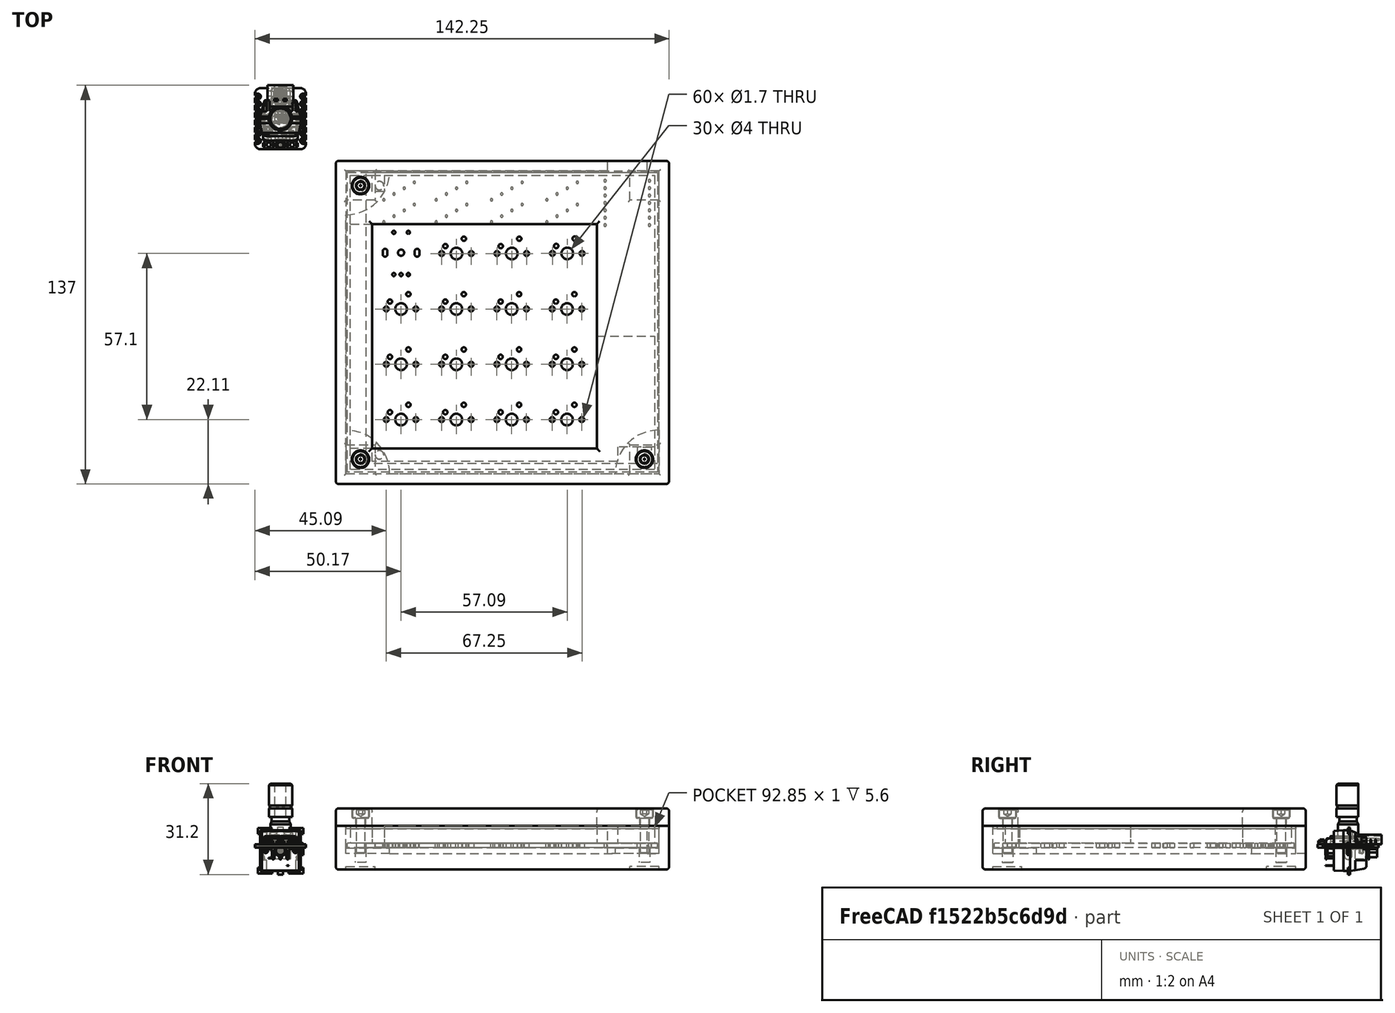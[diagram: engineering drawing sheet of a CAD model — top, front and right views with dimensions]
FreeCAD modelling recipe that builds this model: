
FCSTD DOCUMENT  (FreeCAD 1.0R39109 (Git))
Label: case
License: All rights reserved
LicenseURL: http://en.wikipedia.org/wiki/All_rights_reserved
objects: App::Part×69, Part::Feature×68, Sketcher::SketchObject×13, PartDesign::Pad×10, Part::FeaturePython×3, PartDesign::Fillet×3, PartDesign::ShapeBinder×2, PartDesign::Hole×2, PartDesign::Body×2, PartDesign::Pocket×1
note: 149 computed .brp shape members not serialized (recipe doc carries the construction recipe); baked Part::Feature solids carry a one-line shape summary decoded from their .brp

FEATURE [PartDesign::ShapeBinder] ShapeBinder
  TraceSupport = false
FEATURE [Sketcher::SketchObject] Sketch
  ArcFitTolerance = 1e-06
  AttachmentSupport = -> [XY_Plane]
  ExternalGeometry = -> [ShapeBinder]
  FullyConstrained = true
  MakeInternals = false
  MapMode = 5
  sketch-geometry (26):
    g0: LineSegment StartX=19 StartY=-14.5 StartZ=0 EndX=19 EndY=-125.5 EndZ=0
    g1: LineSegment StartX=19 StartY=-125.5 StartZ=0 EndX=133.5 EndY=-125.5 EndZ=0
    g2: LineSegment StartX=133.5 StartY=-125.5 StartZ=0 EndX=133.5 EndY=-14.5 EndZ=0
    g3: LineSegment StartX=133.5 StartY=-14.5 StartZ=0 EndX=125.925 EndY=-14.5 EndZ=0
    g4: LineSegment StartX=22.5 StartY=-18 StartZ=0 EndX=22.5 EndY=-122 EndZ=0
    g5: LineSegment StartX=22.5 StartY=-122 StartZ=0 EndX=130 EndY=-122 EndZ=0
    g6: LineSegment StartX=130 StartY=-122 StartZ=0 EndX=130 EndY=-18 EndZ=0
    g7: LineSegment StartX=130 StartY=-18 StartZ=0 EndX=125.925 EndY=-18 EndZ=0
    g8: LineSegment [constr] StartX=112.425 StartY=-8.5 StartZ=0 EndX=112.425 EndY=-18.5 EndZ=0
    g9: LineSegment [constr] StartX=112.425 StartY=-18.5 StartZ=0 EndX=125.925 EndY=-18.5 EndZ=0
    g10: LineSegment [constr] StartX=125.925 StartY=-18.5 StartZ=0 EndX=125.925 EndY=-8.5 EndZ=0
    g11: LineSegment [constr] StartX=125.925 StartY=-8.5 StartZ=0 EndX=112.425 EndY=-8.5 EndZ=0
    g12: LineSegment [constr] StartX=110.5 StartY=-18.5 StartZ=0 EndX=129.5 EndY=-18.5 EndZ=0
    g13: GeomPoint [constr] X=119.175 Y=-18.5 Z=0
    g14: GeomPoint [constr] X=120 Y=-18.5 Z=0
    g15: GeomPoint [constr] X=127.85 Y=-18.5 Z=0
    g16: LineSegment [constr] StartX=112.425 StartY=-18.5 StartZ=0 EndX=110.5 EndY=-18.5 EndZ=0
    g17: LineSegment [constr] StartX=125.925 StartY=-18.5 StartZ=0 EndX=127.85 EndY=-18.5 EndZ=0
    g18: LineSegment [constr] StartX=110.5 StartY=-18.5 StartZ=0 EndX=112.425 EndY=-18.5 EndZ=0
    g19: LineSegment [constr] StartX=125.925 StartY=-18.5 StartZ=0 EndX=127.85 EndY=-18.5 EndZ=0
    g20: LineSegment [constr] StartX=110.5 StartY=-18.5 StartZ=0 EndX=112.425 EndY=-18.5 EndZ=0
    g21: LineSegment [constr] StartX=125.925 StartY=-18.5 StartZ=0 EndX=127.85 EndY=-18.5 EndZ=0
    g22: LineSegment StartX=112.425 StartY=-14.5 StartZ=0 EndX=19 EndY=-14.5 EndZ=0
    g23: LineSegment StartX=112.425 StartY=-18 StartZ=0 EndX=22.5 EndY=-18 EndZ=0
    g24: LineSegment StartX=112.425 StartY=-18 StartZ=0 EndX=112.425 EndY=-14.5 EndZ=0
    g25: LineSegment StartX=125.925 StartY=-18 StartZ=0 EndX=125.925 EndY=-14.5 EndZ=0
  constraints (69):
    c: Coincident(g0,g1)
    c: Coincident(g1,g2)
    c: Coincident(g2,g3)
    c: Coincident(g22,g0)
    c: Vertical(g0)
    c: Vertical(g2)
    c: Horizontal(g1)
    c: Horizontal(g3)
    c: Distance(g-6,g2) = 4
    c: DistanceX(g0,g-4) = 4
    c: Distance(g3,g-3) = 4
    c: Distance(g-5,g1) = 4
    c: Coincident(g4,g5)
    c: Coincident(g5,g6)
    c: Coincident(g6,g7)
    c: Coincident(g23,g4)
    c: Vertical(g4)
    c: Vertical(g6)
    c: Horizontal(g5)
    c: Horizontal(g7)
    c: DistanceY(g5,g-6) = 0.5
    c: Distance(g-6,g6) = 0.5
    c: Distance(g7,g-3) = 0.5
    c: Distance(g4,g-4) = 0.5
    c: Coincident(g8,g9)
    c: Coincident(g9,g10)
    c: Coincident(g10,g11)
    c: Coincident(g11,g8)
    c: Vertical(g8)
    c: Vertical(g10)
    c: Horizontal(g9)
    c: Horizontal(g11)
    c: PointOnObject(g9,g-3)
    c: DistanceX(g11,g11) = 13.5
    c: PointOnObject(g12,g-3)
    c: Coincident(g12,g-6)
    c: Symmetric(g9,g9,g13)
    c: DistanceX(g12,g12) = 19
    c: Symmetric(g12,g12,g14)
    c: PointOnObject(g15,g12)
    c: DistanceX(g15,g12) = 1.65
    c: Coincident(g16,g8)
    c: Coincident(g16,g12)
    c: Coincident(g17,g9)
    c: Coincident(g17,g15)
    c: Coincident(g18,g12)
    c: Coincident(g18,g8)
    c: Coincident(g19,g9)
    c: Coincident(g19,g15)
    c: PointOnObject(g20,g8)
    c: Horizontal(g20)
    c: PointOnObject(g21,g10)
    c: Horizontal(g21)
    c: Equal(g21,g20)
    c: Coincident(g21,g15)
    c: Coincident(g20,g12)
    c: DistanceY(g8,g8) = 10
    c: PointOnObject(g3,g10)
    c: PointOnObject(g22,g8)
    c: PointOnObject(g7,g10)
    c: PointOnObject(g23,g8)
    c: Coincident(g24,g23)
    c: Coincident(g24,g22)
    c: Coincident(g25,g7)
    c: Coincident(g25,g3)
    c: Horizontal(g22,g3)
    c: Horizontal(g23,g7)
    c: Horizontal(g23)
    c: Horizontal(g22)
FEATURE [PartDesign::Pad] Pad
  Direction = (0,0,1)
  Length = 15
  Length2 = 10
  Midplane = true
  Profile = -> Sketch
  ReferenceAxis = -> Sketch [N_Axis]
  Suppressed = false
  Type = 0
FEATURE [Sketcher::SketchObject] Sketch001
  ArcFitTolerance = 1e-06
  AttachmentSupport = -> [Pad]
  ExternalGeometry = -> [Pad]
  FullyConstrained = true
  MakeInternals = false
  MapMode = 5
  Placement = pos=(0,-122,0) rot=(0,0.707107,0.707107;3.14159rad)
  sketch-geometry (5):
    g0: GeomPoint X=0 Y=-2 Z=0
    g1: LineSegment StartX=-130 StartY=-7.5 StartZ=0 EndX=-22.5 EndY=-7.5 EndZ=0
    g2: LineSegment StartX=-22.5 StartY=-7.5 StartZ=0 EndX=-22.5 EndY=-2 EndZ=0
    g3: LineSegment StartX=-22.5 StartY=-2 StartZ=0 EndX=-130 EndY=-2 EndZ=0
    g4: LineSegment StartX=-130 StartY=-2 StartZ=0 EndX=-130 EndY=-7.5 EndZ=0
  constraints (13):
    c: PointOnObject(g0,g-2)
    c: DistanceY(g0,g-1) = 2
    c: Coincident(g1,g2)
    c: Coincident(g2,g3)
    c: Coincident(g3,g4)
    c: Coincident(g4,g1)
    c: Horizontal(g1)
    c: Horizontal(g3)
    c: Vertical(g2)
    c: Vertical(g4)
    c: Coincident(g1,g-3)
    c: PointOnObject(g2,g-4)
    c: Horizontal(g0,g2)
FEATURE [PartDesign::Pad] Pad001
  BaseFeature = -> Pad
  Direction = (0,1,-2e-16)
  Length = 10
  Length2 = 10
  Profile = -> Sketch001
  ReferenceAxis = -> Sketch001 [N_Axis]
  Suppressed = false
  Type = 3
  UpToFace = -> Pad [Face2]
FEATURE [Sketcher::SketchObject] Sketch002
  ArcFitTolerance = 1e-06
  AttachmentSupport = -> [Pad001]
  ExternalGeometry = -> [Pad001]
  FullyConstrained = true
  MakeInternals = false
  MapMode = 5
  Placement = pos=(0,-4e-16,-2) rot=(0,0,1;0rad)
  sketch-geometry (9):
    g0: ArcOfCircle CenterX=130 CenterY=-122 CenterZ=0 NormalX=0 NormalY=0 NormalZ=1 AngleXU=0 Radius=15 StartAngle=1.5708 EndAngle=3.14159
    g1: ArcOfCircle CenterX=22.5 CenterY=-122 CenterZ=0 NormalX=0 NormalY=0 NormalZ=1 AngleXU=0 Radius=15 StartAngle=0 EndAngle=1.5708
    g2: ArcOfCircle CenterX=22.5 CenterY=-18 CenterZ=0 NormalX=0 NormalY=0 NormalZ=1 AngleXU=0 Radius=15 StartAngle=4.71239 EndAngle=6.28319
    g3: LineSegment StartX=37.5 StartY=-18 StartZ=0 EndX=22.5 EndY=-18 EndZ=0
    g4: LineSegment StartX=22.5 StartY=-18 StartZ=0 EndX=22.5 EndY=-33 EndZ=0
    g5: LineSegment StartX=22.5 StartY=-122 StartZ=0 EndX=22.5 EndY=-107 EndZ=0
    g6: LineSegment StartX=22.5 StartY=-122 StartZ=0 EndX=37.5 EndY=-122 EndZ=0
    g7: LineSegment StartX=130 StartY=-107 StartZ=0 EndX=130 EndY=-122 EndZ=0
    g8: LineSegment StartX=115 StartY=-122 StartZ=0 EndX=130 EndY=-122 EndZ=0
  constraints (24):
    c: Coincident(g0,g-6)
    c: PointOnObject(g0,g-6)
    c: PointOnObject(g0,g-5)
    c: Radius(g1) = 15
    c: Angle(g1) = 1.5708
    c: Coincident(g1,g-5)
    c: PointOnObject(g1,g-5)
    c: Equal(g0,g1)
    c: Coincident(g2,g-4)
    c: PointOnObject(g2,g-3)
    c: PointOnObject(g2,g-4)
    c: Equal(g2,g1)
    c: Coincident(g2,g3)
    c: Coincident(g3,g2)
    c: Coincident(g3,g4)
    c: Coincident(g4,g2)
    c: Coincident(g5,g1)
    c: Coincident(g5,g1)
    c: Coincident(g6,g1)
    c: Coincident(g6,g1)
    c: Coincident(g7,g0)
    c: Coincident(g7,g0)
    c: Coincident(g8,g0)
    c: Coincident(g8,g0)
FEATURE [PartDesign::Pad] Pad002
  BaseFeature = -> Pad001
  Direction = (0,0,1)
  Length = 1.9
  Length2 = 10
  Profile = -> Sketch002
  ReferenceAxis = -> Sketch002 [N_Axis]
  Suppressed = false
  Type = 0
FEATURE [Sketcher::SketchObject] Sketch003
  ArcFitTolerance = 1e-06
  AttachmentSupport = -> [Pad002]
  ExternalGeometry = -> [Pad002]
  FullyConstrained = true
  MakeInternals = false
  MapMode = 5
  Placement = pos=(0,0,-0.1) rot=(0,0,1;0rad)
  sketch-geometry (3):
    g0: Circle CenterX=27.5 CenterY=-23 CenterZ=0 NormalX=0 NormalY=0 NormalZ=1 AngleXU=0 Radius=1.5
    g1: Circle CenterX=27.5 CenterY=-117 CenterZ=0 NormalX=0 NormalY=0 NormalZ=1 AngleXU=0 Radius=1.5
    g2: Circle CenterX=125 CenterY=-117 CenterZ=0 NormalX=0 NormalY=0 NormalZ=1 AngleXU=0 Radius=1.5
  constraints (9):
    c: DistanceY(g0,g-5) = 5
    c: DistanceX(g-5,g0) = 5
    c: Horizontal(g2,g1)
    c: Vertical(g1,g0)
    c: Distance(g1,g-6) = 5
    c: Distance(g2,g-7) = 5
    c: Diameter(g2) = 3
    c: Equal(g2,g1)
    c: Equal(g1,g0)
FEATURE [Part::Feature] Part__Feature034  label="D_DO-35_SOD27_P7.62mm_Horizontal032"
  shape: bbox 8.244 x 2.165 x 5.082 mm, 16 faces, 2 solids (baked)
FEATURE [App::Part] D_DO_35_SOD27_P7_62mm_Horizontal016  label="D_DO-35_SOD27_P7.62mm_Horizontal033"
  Group = -> [Part__Feature034]
  Origin = -> Origin035
  Placement = pos=(53.5,-35.5,1.65) rot=(0,0,1;1.5708rad)
FEATURE [Part::Feature] Part__Feature035  label="cherry mx v043"
  shape: bbox 15.64 x 17.69 x 16.33 mm, 129 faces, 8 solids (baked)
FEATURE [App::Part] cherryMX015
  Group = -> [Part__Feature035]
  Origin = -> Origin036
  Placement = pos=(79.46,-104.31,6.65) rot=(1,0,0;1.5708rad)
FEATURE [Part::Feature] Part__Feature036  label="D_DO-35_SOD27_P7.62mm_Horizontal034"
  shape: bbox 8.244 x 2.165 x 5.082 mm, 16 faces, 2 solids (baked)
FEATURE [App::Part] D_DO_35_SOD27_P7_62mm_Horizontal017  label="D_DO-35_SOD27_P7.62mm_Horizontal035"
  Group = -> [Part__Feature036]
  Origin = -> Origin037
  Placement = pos=(83,-29.5,1.65) rot=(0,0,1;1.5708rad)
FEATURE [Part::Feature] Part__Feature037  label="D_DO-35_SOD27_P7.62mm_Horizontal036"
  shape: bbox 8.244 x 2.165 x 5.082 mm, 16 faces, 2 solids (baked)
FEATURE [App::Part] D_DO_35_SOD27_P7_62mm_Horizontal018  label="D_DO-35_SOD27_P7.62mm_Horizontal037"
  Group = -> [Part__Feature037]
  Origin = -> Origin038
  Placement = pos=(64,-29.5,1.65) rot=(0,0,1;1.5708rad)
FEATURE [Part::Feature] Part__Feature038  label="D_DO-35_SOD27_P7.62mm_Horizontal038"
  shape: bbox 8.244 x 2.165 x 5.082 mm, 16 faces, 2 solids (baked)
FEATURE [App::Part] D_DO_35_SOD27_P7_62mm_Horizontal019  label="D_DO-35_SOD27_P7.62mm_Horizontal039"
  Group = -> [Part__Feature038]
  Origin = -> Origin039
  Placement = pos=(39,-33.5,1.65) rot=(0,0,1;1.5708rad)
FEATURE [Part::Feature] Part__Feature039  label="D_DO-35_SOD27_P7.62mm_Horizontal040"
  shape: bbox 8.244 x 2.165 x 5.082 mm, 16 faces, 2 solids (baked)
FEATURE [App::Part] D_DO_35_SOD27_P7_62mm_Horizontal020  label="D_DO-35_SOD27_P7.62mm_Horizontal041"
  Group = -> [Part__Feature039]
  Origin = -> Origin040
  Placement = pos=(57,-33.5,1.65) rot=(0,0,1;1.5708rad)
FEATURE [Part::Feature] Part__Feature040  label="cherry mx v044"
  shape: bbox 15.64 x 17.69 x 16.33 mm, 129 faces, 8 solids (baked)
FEATURE [App::Part] cherryMX016
  Group = -> [Part__Feature040]
  Origin = -> Origin041
  Placement = pos=(79.5,-47.25,6.65) rot=(1,0,0;1.5708rad)
FEATURE [Part::Feature] Part__Feature041  label="cherry mx v045"
  shape: bbox 15.64 x 17.69 x 16.33 mm, 129 faces, 8 solids (baked)
FEATURE [App::Part] cherryMX017
  Group = -> [Part__Feature041]
  Origin = -> Origin042
  Placement = pos=(79.46,-85.31,6.65) rot=(1,0,0;1.5708rad)
FEATURE [Part::Feature] Part__Feature042  label="D_DO-35_SOD27_P7.62mm_Horizontal042"
  shape: bbox 8.244 x 2.165 x 5.082 mm, 16 faces, 2 solids (baked)
FEATURE [App::Part] D_DO_35_SOD27_P7_62mm_Horizontal021  label="D_DO-35_SOD27_P7.62mm_Horizontal043"
  Group = -> [Part__Feature042]
  Origin = -> Origin043
  Placement = pos=(98.5,-31.5,1.65) rot=(0,0,1;1.5708rad)
FEATURE [Part::Feature] Part__Feature043  label="D_DO-35_SOD27_P7.62mm_Horizontal044"
  shape: bbox 8.244 x 2.165 x 5.082 mm, 16 faces, 2 solids (baked)
FEATURE [App::Part] D_DO_35_SOD27_P7_62mm_Horizontal022  label="D_DO-35_SOD27_P7.62mm_Horizontal045"
  Group = -> [Part__Feature043]
  Origin = -> Origin044
  Placement = pos=(60.5,-31.5,1.65) rot=(0,0,1;1.5708rad)
FEATURE [Part::Feature] Part__Feature044  label="D_DO-35_SOD27_P7.62mm_Horizontal046"
  shape: bbox 8.244 x 2.165 x 5.082 mm, 16 faces, 2 solids (baked)
FEATURE [App::Part] D_DO_35_SOD27_P7_62mm_Horizontal023  label="D_DO-35_SOD27_P7.62mm_Horizontal047"
  Group = -> [Part__Feature044]
  Origin = -> Origin045
  Placement = pos=(46,-29.5,1.65) rot=(0,0,1;1.5708rad)
FEATURE [Part::Feature] Part__Feature045  label="cherry mx v046"
  shape: bbox 15.64 x 17.69 x 16.33 mm, 129 faces, 8 solids (baked)
FEATURE [App::Part] cherryMX018
  Group = -> [Part__Feature045]
  Origin = -> Origin046
  Placement = pos=(60.46,-66.31,6.65) rot=(1,0,0;1.5708rad)
FEATURE [Part::Feature] Part__Feature046  label="cherry mx v047"
  shape: bbox 15.64 x 17.69 x 16.33 mm, 129 faces, 8 solids (baked)
FEATURE [App::Part] cherryMX019
  Group = -> [Part__Feature046]
  Origin = -> Origin047
  Placement = pos=(98.55,-47.21,6.65) rot=(1,0,0;1.5708rad)
FEATURE [Part::Feature] Part__Feature047  label="D_DO-35_SOD27_P7.62mm_Horizontal048"
  shape: bbox 8.244 x 2.165 x 5.082 mm, 16 faces, 2 solids (baked)
FEATURE [App::Part] D_DO_35_SOD27_P7_62mm_Horizontal024  label="D_DO-35_SOD27_P7.62mm_Horizontal049"
  Group = -> [Part__Feature047]
  Origin = -> Origin048
  Placement = pos=(42.5,-31.5,1.65) rot=(0,0,1;1.5708rad)
FEATURE [Part::Feature] Part__Feature048  label="cherry mx v048"
  shape: bbox 15.64 x 17.69 x 16.33 mm, 129 faces, 8 solids (baked)
FEATURE [App::Part] cherryMX020
  Group = -> [Part__Feature048]
  Origin = -> Origin049
  Placement = pos=(98.46,-85.31,6.65) rot=(1,0,0;1.5708rad)
FEATURE [Part::Feature] Part__Feature049  label="D_DO-35_SOD27_P7.62mm_Horizontal050"
  shape: bbox 8.244 x 2.165 x 5.082 mm, 16 faces, 2 solids (baked)
FEATURE [App::Part] D_DO_35_SOD27_P7_62mm_Horizontal025  label="D_DO-35_SOD27_P7.62mm_Horizontal051"
  Group = -> [Part__Feature049]
  Origin = -> Origin050
  Placement = pos=(102,-29.5,1.65) rot=(0,0,1;1.5708rad)
FEATURE [Part::Feature] Part__Feature050  label="D_DO-35_SOD27_P7.62mm_Horizontal052"
  shape: bbox 8.244 x 2.165 x 5.082 mm, 16 faces, 2 solids (baked)
FEATURE [App::Part] D_DO_35_SOD27_P7_62mm_Horizontal026  label="D_DO-35_SOD27_P7.62mm_Horizontal053"
  Group = -> [Part__Feature050]
  Origin = -> Origin051
  Placement = pos=(76,-33.5,1.65) rot=(0,0,1;1.5708rad)
FEATURE [Part::Feature] Part__Feature051  label="Seeed Studio XIAO RP2040 v027"
  shape: bbox 17.5 x 22 x 4.405 mm, 1237 faces, 83 solids (baked)
FEATURE [App::Part] Seeed_Studio_XIAO_RP2041  label="Seeed Studio XIAO RP2041"
  Group = -> [Part__Feature051]
  Origin = -> Origin052
  Placement = pos=(119.12,-28.96,1.65) rot=(0,0,1;0rad)
FEATURE [Part::Feature] Part__Feature052  label="cherry mx v049"
  shape: bbox 15.64 x 17.69 x 16.33 mm, 129 faces, 8 solids (baked)
FEATURE [App::Part] cherryMX021
  Group = -> [Part__Feature052]
  Origin = -> Origin053
  Placement = pos=(41.46,-66.31,6.65) rot=(1,0,0;1.5708rad)
FEATURE [Part::Feature] Part__Feature053  label="D_DO-35_SOD27_P7.62mm_Horizontal054"
  shape: bbox 8.244 x 2.165 x 5.082 mm, 16 faces, 2 solids (baked)
FEATURE [App::Part] D_DO_35_SOD27_P7_62mm_Horizontal027  label="D_DO-35_SOD27_P7.62mm_Horizontal055"
  Group = -> [Part__Feature053]
  Origin = -> Origin054
  Placement = pos=(35.5,-35.5,1.65) rot=(0,0,1;1.5708rad)
FEATURE [Part::Feature] Part__Feature054  label="D_DO-35_SOD27_P7.62mm_Horizontal056"
  shape: bbox 8.244 x 2.165 x 5.082 mm, 16 faces, 2 solids (baked)
FEATURE [App::Part] D_DO_35_SOD27_P7_62mm_Horizontal028  label="D_DO-35_SOD27_P7.62mm_Horizontal057"
  Group = -> [Part__Feature054]
  Origin = -> Origin055
  Placement = pos=(79.5,-31.5,1.65) rot=(0,0,1;1.5708rad)
FEATURE [Part::Feature] Part__Feature055  label="69001"
  shape: bbox 12.85 x 14.9 x 26 mm, 520 faces, 4 solids (baked)
FEATURE [App::Part] SW_TH_EC11G1534415  label="SW-TH_EC11G1534415"
  Group = -> [Part__Feature055]
  Origin = -> Origin056
  Placement = pos=(41.435,-46.305,1.65) rot=(0,0,1;0rad)
FEATURE [Part::Feature] Part__Feature056  label="cherry mx v050"
  shape: bbox 15.64 x 17.69 x 16.33 mm, 129 faces, 8 solids (baked)
FEATURE [App::Part] cherryMX022
  Group = -> [Part__Feature056]
  Origin = -> Origin057
  Placement = pos=(60.5,-47.25,6.65) rot=(1,0,0;1.5708rad)
FEATURE [Part::Feature] Part__Feature057  label="cherry mx v051"
  shape: bbox 15.64 x 17.69 x 16.33 mm, 129 faces, 8 solids (baked)
FEATURE [App::Part] cherryMX023
  Group = -> [Part__Feature057]
  Origin = -> Origin058
  Placement = pos=(41.46,-104.31,6.65) rot=(1,0,0;1.5708rad)
FEATURE [Part::Feature] Part__Feature058  label="cherry mx v052"
  shape: bbox 15.64 x 17.69 x 16.33 mm, 129 faces, 8 solids (baked)
FEATURE [App::Part] cherryMX024
  Group = -> [Part__Feature058]
  Origin = -> Origin059
  Placement = pos=(60.46,-104.31,6.65) rot=(1,0,0;1.5708rad)
FEATURE [Part::Feature] Part__Feature059  label="cherry mx v053"
  shape: bbox 15.64 x 17.69 x 16.33 mm, 129 faces, 8 solids (baked)
FEATURE [App::Part] cherryMX025
  Group = -> [Part__Feature059]
  Origin = -> Origin060
  Placement = pos=(79.46,-66.31,6.65) rot=(1,0,0;1.5708rad)
FEATURE [Part::Feature] Part__Feature060  label="D_DO-35_SOD27_P7.62mm_Horizontal058"
  shape: bbox 8.244 x 2.165 x 5.082 mm, 16 faces, 2 solids (baked)
FEATURE [App::Part] D_DO_35_SOD27_P7_62mm_Horizontal029  label="D_DO-35_SOD27_P7.62mm_Horizontal059"
  Group = -> [Part__Feature060]
  Origin = -> Origin061
  Placement = pos=(95,-33.5,1.65) rot=(0,0,1;1.5708rad)
FEATURE [Part::Feature] Part__Feature061  label="cherry mx v054"
  shape: bbox 15.64 x 17.69 x 16.33 mm, 129 faces, 8 solids (baked)
FEATURE [App::Part] cherryMX026
  Group = -> [Part__Feature061]
  Origin = -> Origin062
  Placement = pos=(41.46,-85.31,6.65) rot=(1,0,0;1.5708rad)
FEATURE [Part::Feature] Part__Feature062  label="cherry mx v055"
  shape: bbox 15.64 x 17.69 x 16.33 mm, 129 faces, 8 solids (baked)
FEATURE [App::Part] cherryMX027
  Group = -> [Part__Feature062]
  Origin = -> Origin063
  Placement = pos=(98.46,-66.31,6.65) rot=(1,0,0;1.5708rad)
FEATURE [Part::Feature] Part__Feature063  label="cherry mx v056"
  shape: bbox 15.64 x 17.69 x 16.33 mm, 129 faces, 8 solids (baked)
FEATURE [App::Part] cherryMX028
  Group = -> [Part__Feature063]
  Origin = -> Origin064
  Placement = pos=(98.46,-104.31,6.65) rot=(1,0,0;1.5708rad)
FEATURE [Part::Feature] Part__Feature064  label="D_DO-35_SOD27_P7.62mm_Horizontal060"
  shape: bbox 8.244 x 2.165 x 5.082 mm, 16 faces, 2 solids (baked)
FEATURE [App::Part] D_DO_35_SOD27_P7_62mm_Horizontal030  label="D_DO-35_SOD27_P7.62mm_Horizontal061"
  Group = -> [Part__Feature064]
  Origin = -> Origin065
  Placement = pos=(72.5,-35.5,1.65) rot=(0,0,1;1.5708rad)
FEATURE [Part::Feature] Part__Feature065  label="cherry mx v057"
  shape: bbox 15.64 x 17.69 x 16.33 mm, 129 faces, 8 solids (baked)
FEATURE [App::Part] cherryMX029
  Group = -> [Part__Feature065]
  Origin = -> Origin066
  Placement = pos=(60.46,-85.31,6.65) rot=(1,0,0;1.5708rad)
FEATURE [Part::Feature] Part__Feature066  label="D_DO-35_SOD27_P7.62mm_Horizontal062"
  shape: bbox 8.244 x 2.165 x 5.082 mm, 16 faces, 2 solids (baked)
FEATURE [App::Part] D_DO_35_SOD27_P7_62mm_Horizontal031  label="D_DO-35_SOD27_P7.62mm_Horizontal063"
  Group = -> [Part__Feature066]
  Origin = -> Origin067
  Placement = pos=(91.5,-35.5,1.65) rot=(0,0,1;1.5708rad)
FEATURE [Part::Feature] Part__Feature067  label="_autosave-hackpad_PCB"
  shape: bbox 106.5 x 103 x 1.6 mm, 144 faces (baked)
FEATURE [App::Part] hackpad_002  label="hackpad 002"
  Group = -> [D_DO_35_SOD27_P7_62mm_Horizontal016,cherryMX015,D_DO_35_SOD27_P7_62mm_Horizontal017,D_DO_35_SOD27_P7_62mm_Horizontal018,D_DO_35_SOD27_P7_62mm_Horizontal019,D_DO_35_SOD27_P7_62mm_Horizontal020,cherryMX016,cherryMX017,D_DO_35_SOD27_P7_62mm_Horizontal021,D_DO_35_SOD27_P7_62mm_Horizontal022,D_DO_35_SOD27_P7_62mm_Horizontal023,cherryMX018,cherryMX019,D_DO_35_SOD27_P7_62mm_Horizontal024,cherryMX020,+19 more]
  Origin = -> Origin068
FEATURE [PartDesign::Hole] Hole
  BaseFeature = -> Pad002
  CustomThreadClearance = 0
  Depth = 5
  DepthType = 0
  Diameter = 3.7
  DrillForDepth = false
  DrillPoint = 0
  DrillPointAngle = 118
  HoleCutCountersinkAngle = 90
  HoleCutCustomValues = false
  HoleCutDepth = 0
  HoleCutDiameter = 6.1
  HoleCutType = 0
  ModelThread = false
  Profile = -> Sketch003
  Suppressed = false
  Tapered = false
  TaperedAngle = 90
  ThreadClass = 0
  ThreadDepth = 5
  ThreadDepthType = 0
  ThreadDirection = 0
  ThreadFit = 2
  ThreadSize = 0
  ThreadType = 0
  Threaded = false
  UseCustomThreadClearance = false
FEATURE [PartDesign::ShapeBinder] ShapeBinder001
  Support = -> [Hole]
  TraceSupport = false
FEATURE [Sketcher::SketchObject] Sketch004
  ArcFitTolerance = 1e-06
  AttachmentSupport = -> [XY_Plane069]
  ExternalGeometry = -> [ShapeBinder001]
  FullyConstrained = false
  MakeInternals = false
  MapMode = 5
  sketch-geometry (18):
    g0: LineSegment StartX=19 StartY=-14.5 StartZ=0 EndX=19 EndY=-125.5 EndZ=0
    g1: LineSegment StartX=19 StartY=-125.5 StartZ=0 EndX=133.5 EndY=-125.5 EndZ=0
    g2: LineSegment StartX=133.5 StartY=-125.5 StartZ=0 EndX=133.5 EndY=-14.5 EndZ=0
    g3: LineSegment StartX=133.5 StartY=-14.5 StartZ=0 EndX=19 EndY=-14.5 EndZ=0
    g4: LineSegment [constr] StartX=91.5037 StartY=-39.2 StartZ=0 EndX=91.5037 EndY=-53.2 EndZ=0
    g5: LineSegment [constr] StartX=91.5037 StartY=-53.2 StartZ=0 EndX=105.796 EndY=-53.2 EndZ=0
    g6: LineSegment [constr] StartX=105.796 StartY=-53.2 StartZ=0 EndX=105.796 EndY=-39.2 EndZ=0
    g7: LineSegment [constr] StartX=105.796 StartY=-39.2 StartZ=0 EndX=91.5037 EndY=-39.2 EndZ=0
    g8: LineSegment [constr] StartX=34.45 StartY=-96.3 StartZ=0 EndX=34.45 EndY=-110.3 EndZ=0
    g9: LineSegment [constr] StartX=34.45 StartY=-110.3 StartZ=0 EndX=48.45 EndY=-110.3 EndZ=0
    g10: LineSegment [constr] StartX=48.45 StartY=-110.3 StartZ=0 EndX=48.45 EndY=-96.3 EndZ=0
    g11: LineSegment [constr] StartX=48.45 StartY=-96.3 StartZ=0 EndX=34.45 EndY=-96.3 EndZ=0
    g12: GeomPoint [constr] X=41.45 Y=-103.3 Z=0
    g13: GeomPoint [constr] X=98.65 Y=-46.2 Z=0
    g14: LineSegment StartX=31.45 StartY=-36.2 StartZ=0 EndX=31.45 EndY=-113.3 EndZ=0
    g15: LineSegment StartX=31.45 StartY=-113.3 StartZ=0 EndX=108.65 EndY=-113.3 EndZ=0
    g16: LineSegment StartX=108.65 StartY=-113.3 StartZ=0 EndX=108.65 EndY=-36.2 EndZ=0
    g17: LineSegment StartX=108.65 StartY=-36.2 StartZ=0 EndX=31.45 EndY=-36.2 EndZ=0
  constraints (48):
    c: Coincident(g0,g1)
    c: Coincident(g1,g2)
    c: Coincident(g2,g3)
    c: Coincident(g3,g0)
    c: Vertical(g0)
    c: Vertical(g2)
    c: Horizontal(g1)
    c: Horizontal(g3)
    c: Distance(g0,g2) = 114.5
    c: Distance(g1,g3) = 111
    c: Coincident(g0,g-4)
    c: Coincident(g4,g5)
    c: Coincident(g5,g6)
    c: Coincident(g6,g7)
    c: Coincident(g7,g4)
    c: Vertical(g4)
    c: Vertical(g6)
    c: Horizontal(g5)
    c: Horizontal(g7)
    c: Coincident(g8,g9)
    c: Coincident(g9,g10)
    c: Coincident(g10,g11)
    c: Coincident(g11,g8)
    c: Vertical(g8)
    c: Vertical(g10)
    c: Horizontal(g9)
    c: Horizontal(g11)
    c: Symmetric(g4,g5,g13)
    c: DistanceY(g13,g-1) = 46.2
    c: DistanceX(g-1,g13) = 98.65
    c: DistanceY(g12,g13) = 57.1
    c: DistanceX(g12,g13) = 57.2
    c: Symmetric(g9,g8,g12)
    c: DistanceY(g6,g6) = 14
    c: DistanceY(g10,g10) = 14
    c: Equal(g11,g10)
    c: Coincident(g14,g15)
    c: Coincident(g15,g16)
    c: Coincident(g16,g17)
    c: Coincident(g17,g14)
    c: Vertical(g14)
    c: Vertical(g16)
    c: Horizontal(g15)
    c: Horizontal(g17)
    c: Distance(g12,g14) = 10
    c: Distance(g12,g15) = 10
    c: Distance(g13,g17) = 10
    c: Distance(g13,g16) = 10
FEATURE [PartDesign::Pad] Pad003
  Direction = (0,0,1)
  Length = 6
  Length2 = 10
  Profile = -> Sketch004
  ReferenceAxis = -> Sketch004 [N_Axis]
  Suppressed = false
  Type = 0
FEATURE [Sketcher::SketchObject] Sketch005
  ArcFitTolerance = 1e-06
  AttachmentSupport = -> [Pad003]
  ExternalGeometry = -> [Pad003,ShapeBinder001]
  FullyConstrained = true
  MakeInternals = false
  MapMode = 5
  Placement = pos=(0,0,6) rot=(0,0,1;0rad)
  sketch-geometry (3):
    g0: Circle CenterX=27.5 CenterY=-23 CenterZ=0 NormalX=0 NormalY=0 NormalZ=1 AngleXU=0 Radius=1.85
    g1: Circle CenterX=27.5 CenterY=-117 CenterZ=0 NormalX=0 NormalY=0 NormalZ=1 AngleXU=0 Radius=1.85
    g2: Circle CenterX=125 CenterY=-117 CenterZ=0 NormalX=0 NormalY=0 NormalZ=1 AngleXU=0 Radius=1.85
  constraints (6):
    c: Coincident(g0,g-4)
    c: Equal(g0,g-4)
    c: Coincident(g1,g-6)
    c: Equal(g1,g-6)
    c: Coincident(g2,g-5)
    c: Equal(g2,g-5)
FEATURE [PartDesign::Hole] Hole001
  BaseFeature = -> Pad003
  CustomThreadClearance = 0
  Depth = 25
  DepthType = 0
  Diameter = 3.4
  DrillForDepth = false
  DrillPoint = 1
  DrillPointAngle = 118
  HoleCutCountersinkAngle = 90
  HoleCutCustomValues = false
  HoleCutDepth = 3.4
  HoleCutDiameter = 6
  HoleCutType = 5
  ModelThread = false
  Profile = -> Sketch005
  Suppressed = false
  Tapered = false
  TaperedAngle = 90
  ThreadClass = 0
  ThreadDepth = 25
  ThreadDepthType = 0
  ThreadDirection = 0
  ThreadFit = 0
  ThreadSize = 9
  ThreadType = 1
  Threaded = false
  UseCustomThreadClearance = false
FEATURE [Sketcher::SketchObject] Sketch006
  ArcFitTolerance = 1e-06
  AttachmentSupport = -> [Hole001]
  ExternalGeometry = -> [Hole001]
  FullyConstrained = true
  MakeInternals = false
  MapMode = 5
  Placement = pos=(0,0,0) rot=(1,0,0;3.14159rad)
  sketch-geometry (8):
    g0: LineSegment StartX=22.5 StartY=122 StartZ=0 EndX=22.5 EndY=18 EndZ=0
    g1: LineSegment StartX=22.5 StartY=18 StartZ=0 EndX=130 EndY=18 EndZ=0
    g2: LineSegment StartX=130 StartY=18 StartZ=0 EndX=130 EndY=122 EndZ=0
    g3: LineSegment StartX=130 StartY=122 StartZ=0 EndX=22.5 EndY=122 EndZ=0
    g4: LineSegment StartX=24 StartY=120.5 StartZ=0 EndX=24 EndY=19.5 EndZ=0
    g5: LineSegment StartX=24 StartY=19.5 StartZ=0 EndX=128.5 EndY=19.5 EndZ=0
    g6: LineSegment StartX=128.5 StartY=19.5 StartZ=0 EndX=128.5 EndY=120.5 EndZ=0
    g7: LineSegment StartX=128.5 StartY=120.5 StartZ=0 EndX=24 EndY=120.5 EndZ=0
  constraints (24):
    c: Coincident(g0,g1)
    c: Coincident(g1,g2)
    c: Coincident(g2,g3)
    c: Coincident(g3,g0)
    c: Vertical(g0)
    c: Vertical(g2)
    c: Horizontal(g1)
    c: Horizontal(g3)
    c: DistanceX(g1,g1) = 107.5
    c: DistanceY(g2,g2) = 104
    c: Distance(g0,g-6) = 3.5
    c: Distance(g-6,g1) = 3.5
    c: Coincident(g4,g5)
    c: Coincident(g5,g6)
    c: Coincident(g6,g7)
    c: Coincident(g7,g4)
    c: Vertical(g4)
    c: Vertical(g6)
    c: Horizontal(g5)
    c: Horizontal(g7)
    c: Distance(g5,g1) = 1.5
    c: Distance(g2,g6) = 1.5
    c: Distance(g0,g4) = 1.5
    c: Distance(g3,g7) = 1.5
FEATURE [PartDesign::Pad] Pad004
  BaseFeature = -> Hole001
  Direction = (0,0,-1)
  Length = 1
  Length2 = 10
  Profile = -> Sketch006
  ReferenceAxis = -> Sketch006 [N_Axis]
  Refine = true
  Suppressed = false
  Type = 0
FEATURE [Sketcher::SketchObject] Sketch007
  ArcFitTolerance = 1e-06
  AttachmentSupport = -> [Hole]
  ExternalGeometry = -> [Hole]
  FullyConstrained = true
  MakeInternals = false
  MapMode = 5
  Placement = pos=(0,-1.7e-15,-7.5) rot=(1,0,0;3.14159rad)
  sketch-geometry (16):
    g0: LineSegment StartX=22.5 StartY=122 StartZ=0 EndX=22.5 EndY=112 EndZ=0
    g1: LineSegment StartX=22.5 StartY=112 StartZ=0 EndX=32.5 EndY=112 EndZ=0
    g2: LineSegment StartX=32.5 StartY=112 StartZ=0 EndX=32.5 EndY=122 EndZ=0
    g3: LineSegment StartX=32.5 StartY=122 StartZ=0 EndX=22.5 EndY=122 EndZ=0
    g4: LineSegment StartX=130 StartY=122 StartZ=0 EndX=120 EndY=122 EndZ=0
    g5: LineSegment StartX=120 StartY=122 StartZ=0 EndX=120 EndY=112 EndZ=0
    g6: LineSegment StartX=120 StartY=112 StartZ=0 EndX=130 EndY=112 EndZ=0
    g7: LineSegment StartX=130 StartY=112 StartZ=0 EndX=130 EndY=122 EndZ=0
    g8: LineSegment StartX=130 StartY=18 StartZ=0 EndX=130 EndY=28 EndZ=0
    g9: LineSegment StartX=130 StartY=28 StartZ=0 EndX=120 EndY=28 EndZ=0
    g10: LineSegment StartX=120 StartY=28 StartZ=0 EndX=120 EndY=18 EndZ=0
    g11: LineSegment StartX=120 StartY=18 StartZ=0 EndX=130 EndY=18 EndZ=0
    g12: LineSegment StartX=22.5 StartY=18 StartZ=0 EndX=32.5 EndY=18 EndZ=0
    g13: LineSegment StartX=32.5 StartY=18 StartZ=0 EndX=32.5 EndY=28 EndZ=0
    g14: LineSegment StartX=32.5 StartY=28 StartZ=0 EndX=22.5 EndY=28 EndZ=0
    g15: LineSegment StartX=22.5 StartY=28 StartZ=0 EndX=22.5 EndY=18 EndZ=0
  constraints (44):
    c: Coincident(g0,g1)
    c: Coincident(g1,g2)
    c: Coincident(g2,g3)
    c: Coincident(g3,g0)
    c: Vertical(g0)
    c: Vertical(g2)
    c: Horizontal(g1)
    c: Horizontal(g3)
    c: Distance(g0,g2) = 10
    c: Distance(g1,g3) = 10
    c: Coincident(g0,g-4)
    c: Coincident(g4,g5)
    c: Coincident(g5,g6)
    c: Coincident(g6,g7)
    c: Coincident(g7,g4)
    c: Horizontal(g4)
    c: Horizontal(g6)
    c: Vertical(g5)
    c: Vertical(g7)
    c: Distance(g5,g7) = 10
    c: Distance(g4,g6) = 10
    c: Coincident(g4,g-6)
    c: Coincident(g8,g9)
    c: Coincident(g9,g10)
    c: Coincident(g10,g11)
    c: Coincident(g11,g8)
    c: Vertical(g8)
    c: Vertical(g10)
    c: Horizontal(g9)
    c: Horizontal(g11)
    c: Distance(g8,g10) = 10
    c: Distance(g9,g11) = 10
    c: Coincident(g8,g-7)
    c: Coincident(g12,g13)
    c: Coincident(g13,g14)
    c: Coincident(g14,g15)
    c: Coincident(g15,g12)
    c: Horizontal(g12)
    c: Horizontal(g14)
    c: Vertical(g13)
    c: Vertical(g15)
    c: Distance(g13,g15) = 10
    c: Distance(g12,g14) = 10
    c: Coincident(g12,g-4)
FEATURE [PartDesign::Pocket] Pocket
  BaseFeature = -> Hole
  Direction = (0,0,1)
  Length = 1
  Length2 = 5
  Profile = -> Sketch007
  ReferenceAxis = -> Sketch007 [N_Axis]
  Refine = true
  Suppressed = false
  Type = 0
FEATURE [Part::FeaturePython] Screw  label="M3x12-Screw"  # WARN: FeaturePython — macro-defined, semantics opaque (R4)
  Diameter = 4
  Invert = false
  LeftHanded = false
  Length = 4
  LengthCustom = 12
  MatchOuter = false
  OffsetAngle = 0
  Placement = pos=(27.5,-23,10) rot=(0,0,1;0rad)
  Thread = false
  Type = 74
FEATURE [Part::FeaturePython] Screw001  label="M3x12-Screw007"  # WARN: FeaturePython — macro-defined, semantics opaque (R4)
  Diameter = 4
  Invert = false
  LeftHanded = false
  Length = 4
  LengthCustom = 12
  MatchOuter = false
  OffsetAngle = 0
  Placement = pos=(27.5,-117,10) rot=(0,0,1;0rad)
  Thread = false
  Type = 74
FEATURE [Part::FeaturePython] Screw002  label="M3x12-Screw006"  # WARN: FeaturePython — macro-defined, semantics opaque (R4)
  Diameter = 4
  Invert = false
  LeftHanded = false
  Length = 4
  LengthCustom = 12
  MatchOuter = false
  OffsetAngle = 0
  Placement = pos=(125,-117,10) rot=(0,0,1;0rad)
  Thread = false
  Type = 74
FEATURE [PartDesign::Fillet] Fillet
  Base = -> Pocket [Edge8,Edge9,Edge5,Edge6,Edge3,Edge63,Edge2,Edge1]
  BaseFeature = -> Pocket
  Radius = 1
  SupportTransform = false
  Suppressed = false
  UseAllEdges = false
FEATURE [PartDesign::Fillet] Fillet001
  Base = -> Fillet [Edge85,Edge84,Edge83,Face20]
  BaseFeature = -> Fillet
  Radius = 0.5
  SupportTransform = false
  Suppressed = false
  UseAllEdges = false
FEATURE [PartDesign::Body] Body
  AllowCompound = false
  Group = -> [ShapeBinder,Sketch,Pad,Sketch001,Pad001,Sketch002,Pad002,Sketch003,Hole,Sketch007,Pocket,Fillet,Fillet001]
  Origin = -> Origin
  Tip = -> Fillet001
FEATURE [PartDesign::Fillet] Fillet002
  Base = -> Pad004 [Edge8,Edge5,Edge1,Edge2,Edge20,Edge18,Edge21,Edge19,Edge4,Edge7,Edge10,Edge16]
  BaseFeature = -> Pad004
  Radius = 1
  SupportTransform = false
  Suppressed = false
  UseAllEdges = false
FEATURE [App::Part] Part
  Group = -> [Screw002,Screw001,Screw]
  Origin = -> Origin070
FEATURE [Sketcher::SketchObject] Sketch008
  ArcFitTolerance = 1e-06
  AttachmentSupport = -> [Fillet002]
  ExternalGeometry = -> [Fillet002]
  FullyConstrained = true
  MakeInternals = false
  MapMode = 5
  Placement = pos=(0,0,0) rot=(1,0,0;3.14159rad)
  sketch-geometry (12):
    g0: LineSegment StartX=31.45 StartY=36.2 StartZ=0 EndX=31.45 EndY=113.3 EndZ=0
    g1: LineSegment StartX=31.45 StartY=113.3 StartZ=0 EndX=108.65 EndY=113.3 EndZ=0
    g2: LineSegment StartX=108.65 StartY=113.3 StartZ=0 EndX=108.65 EndY=74.75 EndZ=0
    g3: LineSegment StartX=108.65 StartY=74.75 StartZ=0 EndX=128.5 EndY=74.75 EndZ=0
    g4: LineSegment StartX=128.5 StartY=74.75 StartZ=0 EndX=128.5 EndY=112.75 EndZ=0
    g5: LineSegment StartX=128.5 StartY=112.75 StartZ=0 EndX=115.75 EndY=112.75 EndZ=0
    g6: LineSegment StartX=115.75 StartY=112.75 StartZ=0 EndX=115.75 EndY=117.75 EndZ=0
    g7: LineSegment StartX=115.75 StartY=117.75 StartZ=0 EndX=31.45 EndY=117.75 EndZ=0
    g8: LineSegment StartX=31.45 StartY=117.75 StartZ=0 EndX=31.45 EndY=113.3 EndZ=0
    g9: LineSegment StartX=31.45 StartY=113.3 StartZ=0 EndX=24 EndY=113.3 EndZ=0
    g10: LineSegment StartX=24 StartY=113.3 StartZ=0 EndX=24 EndY=36.2 EndZ=0
    g11: LineSegment StartX=24 StartY=36.2 StartZ=0 EndX=31.45 EndY=36.2 EndZ=0
  constraints (31):
    c: Coincident(g-4,g0)
    c: Coincident(g0,g-4)
    c: Coincident(g0,g1)
    c: Coincident(g1,g-5)
    c: Coincident(g1,g2)
    c: Symmetric(g-5,g-5,g2)
    c: Coincident(g2,g3)
    c: Horizontal(g3)
    c: PointOnObject(g3,g-7)
    c: Coincident(g3,g4)
    c: PointOnObject(g4,g-7)
    c: Coincident(g4,g5)
    c: Horizontal(g5)
    c: Coincident(g5,g6)
    c: Vertical(g6)
    c: Coincident(g6,g7)
    c: Horizontal(g7)
    c: Coincident(g7,g8)
    c: Coincident(g8,g0)
    c: Vertical(g8)
    c: Coincident(g0,g9)
    c: PointOnObject(g9,g-9)
    c: Horizontal(g9)
    c: Coincident(g9,g10)
    c: PointOnObject(g10,g-9)
    c: Coincident(g10,g11)
    c: Coincident(g11,g0)
    c: Horizontal(g11)
    c: DistanceY(g6,g6) = 5
    c: DistanceX(g5,g5) = 12.75
    c: DistanceY(g4,g4) = 38
FEATURE [Part::Feature] Part__Feature  label="D_DO-35_SOD27_P7.62mm_Horizontal"
  shape: bbox 8.244 x 2.165 x 5.082 mm, 16 faces, 2 solids (baked)
FEATURE [App::Part] D_DO_35_SOD27_P7_62mm_Horizontal  label="D_DO-35_SOD27_P7.62mm_Horizontal064"
  Group = -> [Part__Feature]
  Origin = -> Origin071
  Placement = pos=(53.5,-35.5,1.65) rot=(0,0,1;1.5708rad)
FEATURE [Part::Feature] Part__Feature068  label="cherry mx v28"
  shape: bbox 15.64 x 17.69 x 16.33 mm, 129 faces, 8 solids (baked)
FEATURE [App::Part] cherryMX
  Group = -> [Part__Feature068]
  Origin = -> Origin072
  Placement = pos=(79.46,-104.31,6.65) rot=(1,0,0;1.5708rad)
FEATURE [Part::Feature] Part__Feature069  label="D_DO-35_SOD27_P7.62mm_Horizontal065"
  shape: bbox 8.244 x 2.165 x 5.082 mm, 16 faces, 2 solids (baked)
FEATURE [App::Part] D_DO_35_SOD27_P7_62mm_Horizontal032  label="D_DO-35_SOD27_P7.62mm_Horizontal066"
  Group = -> [Part__Feature069]
  Origin = -> Origin073
  Placement = pos=(83,-29.5,1.65) rot=(0,0,1;1.5708rad)
FEATURE [Part::Feature] Part__Feature070  label="D_DO-35_SOD27_P7.62mm_Horizontal067"
  shape: bbox 8.244 x 2.165 x 5.082 mm, 16 faces, 2 solids (baked)
FEATURE [App::Part] D_DO_35_SOD27_P7_62mm_Horizontal033  label="D_DO-35_SOD27_P7.62mm_Horizontal068"
  Group = -> [Part__Feature070]
  Origin = -> Origin074
  Placement = pos=(64,-29.5,1.65) rot=(0,0,1;1.5708rad)
FEATURE [Part::Feature] Part__Feature071  label="D_DO-35_SOD27_P7.62mm_Horizontal069"
  shape: bbox 8.244 x 2.165 x 5.082 mm, 16 faces, 2 solids (baked)
FEATURE [App::Part] D_DO_35_SOD27_P7_62mm_Horizontal034  label="D_DO-35_SOD27_P7.62mm_Horizontal070"
  Group = -> [Part__Feature071]
  Origin = -> Origin075
  Placement = pos=(39,-33.5,1.65) rot=(0,0,1;1.5708rad)
FEATURE [Part::Feature] Part__Feature072  label="D_DO-35_SOD27_P7.62mm_Horizontal071"
  shape: bbox 8.244 x 2.165 x 5.082 mm, 16 faces, 2 solids (baked)
FEATURE [App::Part] D_DO_35_SOD27_P7_62mm_Horizontal035  label="D_DO-35_SOD27_P7.62mm_Horizontal072"
  Group = -> [Part__Feature072]
  Origin = -> Origin076
  Placement = pos=(57,-33.5,1.65) rot=(0,0,1;1.5708rad)
FEATURE [Part::Feature] Part__Feature073  label="cherry mx v058"
  shape: bbox 15.64 x 17.69 x 16.33 mm, 129 faces, 8 solids (baked)
FEATURE [App::Part] cherryMX030
  Group = -> [Part__Feature073]
  Origin = -> Origin077
  Placement = pos=(79.5,-47.25,6.65) rot=(1,0,0;1.5708rad)
FEATURE [Part::Feature] Part__Feature074  label="cherry mx v059"
  shape: bbox 15.64 x 17.69 x 16.33 mm, 129 faces, 8 solids (baked)
FEATURE [App::Part] cherryMX031
  Group = -> [Part__Feature074]
  Origin = -> Origin078
  Placement = pos=(79.46,-85.31,6.65) rot=(1,0,0;1.5708rad)
FEATURE [Part::Feature] Part__Feature075  label="D_DO-35_SOD27_P7.62mm_Horizontal073"
  shape: bbox 8.244 x 2.165 x 5.082 mm, 16 faces, 2 solids (baked)
FEATURE [App::Part] D_DO_35_SOD27_P7_62mm_Horizontal036  label="D_DO-35_SOD27_P7.62mm_Horizontal074"
  Group = -> [Part__Feature075]
  Origin = -> Origin079
  Placement = pos=(98.5,-31.5,1.65) rot=(0,0,1;1.5708rad)
FEATURE [Part::Feature] Part__Feature076  label="D_DO-35_SOD27_P7.62mm_Horizontal075"
  shape: bbox 8.244 x 2.165 x 5.082 mm, 16 faces, 2 solids (baked)
FEATURE [App::Part] D_DO_35_SOD27_P7_62mm_Horizontal037  label="D_DO-35_SOD27_P7.62mm_Horizontal076"
  Group = -> [Part__Feature076]
  Origin = -> Origin080
  Placement = pos=(60.5,-31.5,1.65) rot=(0,0,1;1.5708rad)
FEATURE [Part::Feature] Part__Feature077  label="D_DO-35_SOD27_P7.62mm_Horizontal077"
  shape: bbox 8.244 x 2.165 x 5.082 mm, 16 faces, 2 solids (baked)
FEATURE [App::Part] D_DO_35_SOD27_P7_62mm_Horizontal038  label="D_DO-35_SOD27_P7.62mm_Horizontal078"
  Group = -> [Part__Feature077]
  Origin = -> Origin081
  Placement = pos=(46,-29.5,1.65) rot=(0,0,1;1.5708rad)
FEATURE [Part::Feature] Part__Feature078  label="cherry mx v060"
  shape: bbox 15.64 x 17.69 x 16.33 mm, 129 faces, 8 solids (baked)
FEATURE [App::Part] cherryMX032
  Group = -> [Part__Feature078]
  Origin = -> Origin082
  Placement = pos=(60.46,-66.31,6.65) rot=(1,0,0;1.5708rad)
FEATURE [Part::Feature] Part__Feature079  label="cherry mx v061"
  shape: bbox 15.64 x 17.69 x 16.33 mm, 129 faces, 8 solids (baked)
FEATURE [App::Part] cherryMX033
  Group = -> [Part__Feature079]
  Origin = -> Origin083
  Placement = pos=(98.55,-47.21,6.65) rot=(1,0,0;1.5708rad)
FEATURE [Part::Feature] Part__Feature080  label="D_DO-35_SOD27_P7.62mm_Horizontal079"
  shape: bbox 8.244 x 2.165 x 5.082 mm, 16 faces, 2 solids (baked)
FEATURE [App::Part] D_DO_35_SOD27_P7_62mm_Horizontal039  label="D_DO-35_SOD27_P7.62mm_Horizontal080"
  Group = -> [Part__Feature080]
  Origin = -> Origin084
  Placement = pos=(42.5,-31.5,1.65) rot=(0,0,1;1.5708rad)
FEATURE [Part::Feature] Part__Feature081  label="cherry mx v062"
  shape: bbox 15.64 x 17.69 x 16.33 mm, 129 faces, 8 solids (baked)
FEATURE [App::Part] cherryMX034
  Group = -> [Part__Feature081]
  Origin = -> Origin085
  Placement = pos=(98.46,-85.31,6.65) rot=(1,0,0;1.5708rad)
FEATURE [Part::Feature] Part__Feature082  label="D_DO-35_SOD27_P7.62mm_Horizontal081"
  shape: bbox 8.244 x 2.165 x 5.082 mm, 16 faces, 2 solids (baked)
FEATURE [App::Part] D_DO_35_SOD27_P7_62mm_Horizontal040  label="D_DO-35_SOD27_P7.62mm_Horizontal082"
  Group = -> [Part__Feature082]
  Origin = -> Origin086
  Placement = pos=(102,-29.5,1.65) rot=(0,0,1;1.5708rad)
FEATURE [Part::Feature] Part__Feature083  label="D_DO-35_SOD27_P7.62mm_Horizontal083"
  shape: bbox 8.244 x 2.165 x 5.082 mm, 16 faces, 2 solids (baked)
FEATURE [App::Part] D_DO_35_SOD27_P7_62mm_Horizontal041  label="D_DO-35_SOD27_P7.62mm_Horizontal084"
  Group = -> [Part__Feature083]
  Origin = -> Origin087
  Placement = pos=(76,-33.5,1.65) rot=(0,0,1;1.5708rad)
FEATURE [Part::Feature] Part__Feature084  label="Seeed Studio XIAO RP2040 v26"
  shape: bbox 17.5 x 22 x 4.405 mm, 1237 faces, 83 solids (baked)
FEATURE [App::Part] Seeed_Studio_XIAO_RP2040  label="Seeed Studio XIAO RP2040"
  Group = -> [Part__Feature084]
  Origin = -> Origin088
  Placement = pos=(119.12,-28.96,1.65) rot=(0,0,1;0rad)
FEATURE [Part::Feature] Part__Feature085  label="cherry mx v063"
  shape: bbox 15.64 x 17.69 x 16.33 mm, 129 faces, 8 solids (baked)
FEATURE [App::Part] cherryMX035
  Group = -> [Part__Feature085]
  Origin = -> Origin089
  Placement = pos=(41.46,-66.31,6.65) rot=(1,0,0;1.5708rad)
FEATURE [Part::Feature] Part__Feature086  label="D_DO-35_SOD27_P7.62mm_Horizontal085"
  shape: bbox 8.244 x 2.165 x 5.082 mm, 16 faces, 2 solids (baked)
FEATURE [App::Part] D_DO_35_SOD27_P7_62mm_Horizontal042  label="D_DO-35_SOD27_P7.62mm_Horizontal086"
  Group = -> [Part__Feature086]
  Origin = -> Origin090
  Placement = pos=(35.5,-35.5,1.65) rot=(0,0,1;1.5708rad)
FEATURE [Part::Feature] Part__Feature087  label="D_DO-35_SOD27_P7.62mm_Horizontal087"
  shape: bbox 8.244 x 2.165 x 5.082 mm, 16 faces, 2 solids (baked)
FEATURE [App::Part] D_DO_35_SOD27_P7_62mm_Horizontal043  label="D_DO-35_SOD27_P7.62mm_Horizontal088"
  Group = -> [Part__Feature087]
  Origin = -> Origin091
  Placement = pos=(79.5,-31.5,1.65) rot=(0,0,1;1.5708rad)
FEATURE [Part::Feature] Part__Feature088  label="69"
  shape: bbox 12.85 x 14.9 x 26 mm, 520 faces, 4 solids (baked)
FEATURE [App::Part] SW_TH_EC11G1534414  label="SW-TH_EC11G1534414"
  Group = -> [Part__Feature088]
  Origin = -> Origin092
  Placement = pos=(41.435,-46.305,1.65) rot=(0,0,1;0rad)
FEATURE [Part::Feature] Part__Feature089  label="cherry mx v064"
  shape: bbox 15.64 x 17.69 x 16.33 mm, 129 faces, 8 solids (baked)
FEATURE [App::Part] cherryMX036
  Group = -> [Part__Feature089]
  Origin = -> Origin093
  Placement = pos=(60.5,-47.25,6.65) rot=(1,0,0;1.5708rad)
FEATURE [Part::Feature] Part__Feature090  label="cherry mx v065"
  shape: bbox 15.64 x 17.69 x 16.33 mm, 129 faces, 8 solids (baked)
FEATURE [App::Part] cherryMX037
  Group = -> [Part__Feature090]
  Origin = -> Origin094
  Placement = pos=(41.46,-104.31,6.65) rot=(1,0,0;1.5708rad)
FEATURE [Part::Feature] Part__Feature091  label="cherry mx v066"
  shape: bbox 15.64 x 17.69 x 16.33 mm, 129 faces, 8 solids (baked)
FEATURE [App::Part] cherryMX038
  Group = -> [Part__Feature091]
  Origin = -> Origin095
  Placement = pos=(60.46,-104.31,6.65) rot=(1,0,0;1.5708rad)
FEATURE [Part::Feature] Part__Feature092  label="cherry mx v067"
  shape: bbox 15.64 x 17.69 x 16.33 mm, 129 faces, 8 solids (baked)
FEATURE [App::Part] cherryMX039
  Group = -> [Part__Feature092]
  Origin = -> Origin096
  Placement = pos=(79.46,-66.31,6.65) rot=(1,0,0;1.5708rad)
FEATURE [Part::Feature] Part__Feature093  label="D_DO-35_SOD27_P7.62mm_Horizontal089"
  shape: bbox 8.244 x 2.165 x 5.082 mm, 16 faces, 2 solids (baked)
FEATURE [App::Part] D_DO_35_SOD27_P7_62mm_Horizontal044  label="D_DO-35_SOD27_P7.62mm_Horizontal090"
  Group = -> [Part__Feature093]
  Origin = -> Origin097
  Placement = pos=(95,-33.5,1.65) rot=(0,0,1;1.5708rad)
FEATURE [Part::Feature] Part__Feature094  label="cherry mx v068"
  shape: bbox 15.64 x 17.69 x 16.33 mm, 129 faces, 8 solids (baked)
FEATURE [App::Part] cherryMX040
  Group = -> [Part__Feature094]
  Origin = -> Origin098
  Placement = pos=(41.46,-85.31,6.65) rot=(1,0,0;1.5708rad)
FEATURE [Part::Feature] Part__Feature095  label="cherry mx v069"
  shape: bbox 15.64 x 17.69 x 16.33 mm, 129 faces, 8 solids (baked)
FEATURE [App::Part] cherryMX041
  Group = -> [Part__Feature095]
  Origin = -> Origin099
  Placement = pos=(98.46,-66.31,6.65) rot=(1,0,0;1.5708rad)
FEATURE [Part::Feature] Part__Feature096  label="cherry mx v070"
  shape: bbox 15.64 x 17.69 x 16.33 mm, 129 faces, 8 solids (baked)
FEATURE [App::Part] cherryMX042
  Group = -> [Part__Feature096]
  Origin = -> Origin100
  Placement = pos=(98.46,-104.31,6.65) rot=(1,0,0;1.5708rad)
FEATURE [Part::Feature] Part__Feature097  label="D_DO-35_SOD27_P7.62mm_Horizontal091"
  shape: bbox 8.244 x 2.165 x 5.082 mm, 16 faces, 2 solids (baked)
FEATURE [App::Part] D_DO_35_SOD27_P7_62mm_Horizontal045  label="D_DO-35_SOD27_P7.62mm_Horizontal092"
  Group = -> [Part__Feature097]
  Origin = -> Origin101
  Placement = pos=(72.5,-35.5,1.65) rot=(0,0,1;1.5708rad)
FEATURE [Part::Feature] Part__Feature098  label="cherry mx v071"
  shape: bbox 15.64 x 17.69 x 16.33 mm, 129 faces, 8 solids (baked)
FEATURE [App::Part] cherryMX043
  Group = -> [Part__Feature098]
  Origin = -> Origin102
  Placement = pos=(60.46,-85.31,6.65) rot=(1,0,0;1.5708rad)
FEATURE [Part::Feature] Part__Feature099  label="D_DO-35_SOD27_P7.62mm_Horizontal093"
  shape: bbox 8.244 x 2.165 x 5.082 mm, 16 faces, 2 solids (baked)
FEATURE [App::Part] D_DO_35_SOD27_P7_62mm_Horizontal046  label="D_DO-35_SOD27_P7.62mm_Horizontal094"
  Group = -> [Part__Feature099]
  Origin = -> Origin103
  Placement = pos=(91.5,-35.5,1.65) rot=(0,0,1;1.5708rad)
FEATURE [Part::Feature] Part__Feature100  label="_autosave-hackpad_PCB001"
  shape: bbox 100 x 100 x 1.6 mm, 147 faces (baked)
FEATURE [App::Part] hackpad_1  label="hackpad 1"
  Group = -> [D_DO_35_SOD27_P7_62mm_Horizontal,cherryMX,D_DO_35_SOD27_P7_62mm_Horizontal032,D_DO_35_SOD27_P7_62mm_Horizontal033,D_DO_35_SOD27_P7_62mm_Horizontal034,D_DO_35_SOD27_P7_62mm_Horizontal035,cherryMX030,cherryMX031,D_DO_35_SOD27_P7_62mm_Horizontal036,D_DO_35_SOD27_P7_62mm_Horizontal037,D_DO_35_SOD27_P7_62mm_Horizontal038,cherryMX032,cherryMX033,D_DO_35_SOD27_P7_62mm_Horizontal039,cherryMX034,+19 more]
  Origin = -> Origin104
FEATURE [PartDesign::Pad] Pad005
  BaseFeature = -> Fillet002
  Direction = (0,0,-1)
  Length = 5.9
  Length2 = 10
  Profile = -> Sketch008
  ReferenceAxis = -> Sketch008 [N_Axis]
  Suppressed = false
  Type = 0
FEATURE [Sketcher::SketchObject] Sketch009
  ArcFitTolerance = 1e-06
  AttachmentSupport = -> [Pad005]
  ExternalGeometry = -> [Pad005]
  FullyConstrained = true
  MakeInternals = false
  MapMode = 5
  Placement = pos=(0,0,-5.9) rot=(1,0,0;3.14159rad)
  sketch-geometry (1):
    g0: Circle CenterX=34 CenterY=115.5 CenterZ=0 NormalX=0 NormalY=0 NormalZ=1 AngleXU=0 Radius=1.45
  constraints (3):
    c: Diameter(g0) = 2.9
    c: Distance(g0,g-3) = 2.55
    c: DistanceY(g0,g-3) = 2.25
FEATURE [PartDesign::Pad] Pad006
  BaseFeature = -> Pad005
  Direction = (0,0,-1)
  Length = 1.5
  Length2 = 10
  Profile = -> Sketch009
  ReferenceAxis = -> Sketch009 [N_Axis]
  Suppressed = false
  Type = 0
FEATURE [Sketcher::SketchObject] Sketch010
  ArcFitTolerance = 1e-06
  AttachmentSupport = -> [Pad006]
  ExternalGeometry = -> [Pad006]
  FullyConstrained = true
  MakeInternals = false
  MapMode = 5
  Placement = pos=(0,0,0) rot=(1,0,0;3.14159rad)
  sketch-geometry (4):
    g0: LineSegment StartX=31.45 StartY=19.5 StartZ=0 EndX=35.65 EndY=19.5 EndZ=0
    g1: LineSegment StartX=35.65 StartY=19.5 StartZ=0 EndX=35.65 EndY=25.1 EndZ=0
    g2: LineSegment StartX=35.65 StartY=25.1 StartZ=0 EndX=31.45 EndY=25.1 EndZ=0
    g3: LineSegment StartX=31.45 StartY=25.1 StartZ=0 EndX=31.45 EndY=19.5 EndZ=0
  constraints (12):
    c: Coincident(g0,g1)
    c: Coincident(g1,g2)
    c: Coincident(g2,g3)
    c: Coincident(g3,g0)
    c: Horizontal(g0)
    c: Horizontal(g2)
    c: Vertical(g1)
    c: Vertical(g3)
    c: PointOnObject(g0,g-3)
    c: DistanceX(g0,g0) = 4.2
    c: DistanceY(g3,g3) = 5.6
    c: DistanceX(g-3,g0) = 7.45
FEATURE [PartDesign::Pad] Pad007
  BaseFeature = -> Pad006
  Direction = (0,0,-1)
  Length = 5.9
  Length2 = 10
  Profile = -> Sketch010
  ReferenceAxis = -> Sketch010 [N_Axis]
  Suppressed = false
  Type = 0
FEATURE [Sketcher::SketchObject] Sketch011
  ArcFitTolerance = 1e-06
  AttachmentSupport = -> [Pad007]
  ExternalGeometry = -> [Pad007]
  FullyConstrained = true
  MakeInternals = false
  MapMode = 5
  Placement = pos=(0,0,-5.9) rot=(1,0,0;3.14159rad)
  sketch-geometry (1):
    g0: Circle CenterX=34 CenterY=23 CenterZ=0 NormalX=0 NormalY=0 NormalZ=1 AngleXU=0 Radius=1.45
  constraints (3):
    c: Diameter(g0) = 2.9
    c: DistanceX(g-4,g0) = 2.55
    c: DistanceY(g0,g-4) = 2.1
FEATURE [PartDesign::Pad] Pad008
  BaseFeature = -> Pad007
  Direction = (0,0,-1)
  Length = 1.5
  Length2 = 10
  Profile = -> Sketch011
  ReferenceAxis = -> Sketch011 [N_Axis]
  Suppressed = false
  Type = 0
FEATURE [Sketcher::SketchObject] Sketch012
  ArcFitTolerance = 1e-06
  AttachmentSupport = -> [Pad008]
  FullyConstrained = false
  MakeInternals = false
  MapMode = 5
  Placement = pos=(0,0,2.6) rot=(0,0,1;0rad)
  sketch-geometry (12):
    g0: LineSegment StartX=22.5907 StartY=-17.8671 StartZ=0 EndX=22.5907 EndY=-29.1688 EndZ=0
    g1: LineSegment StartX=22.5907 StartY=-29.1688 StartZ=0 EndX=35.2528 EndY=-29.1688 EndZ=0
    g2: LineSegment StartX=35.2528 StartY=-29.1688 StartZ=0 EndX=35.2528 EndY=-17.8671 EndZ=0
    g3: LineSegment StartX=35.2528 StartY=-17.8671 StartZ=0 EndX=22.5907 EndY=-17.8671 EndZ=0
    g4: LineSegment StartX=21.3289 StartY=-113.983 StartZ=0 EndX=21.3289 EndY=-121.098 EndZ=0
    g5: LineSegment StartX=21.3289 StartY=-121.098 StartZ=0 EndX=31.1657 EndY=-121.098 EndZ=0
    g6: LineSegment StartX=31.1657 StartY=-121.098 StartZ=0 EndX=31.1657 EndY=-113.983 EndZ=0
    g7: LineSegment StartX=31.1657 StartY=-113.983 StartZ=0 EndX=21.3289 EndY=-113.983 EndZ=0
    g8: LineSegment StartX=121.894 StartY=-112.308 StartZ=0 EndX=121.894 EndY=-122.982 EndZ=0
    g9: LineSegment StartX=121.894 StartY=-122.982 StartZ=0 EndX=130.58 EndY=-122.982 EndZ=0
    g10: LineSegment StartX=130.58 StartY=-122.982 StartZ=0 EndX=130.58 EndY=-112.308 EndZ=0
    g11: LineSegment StartX=130.58 StartY=-112.308 StartZ=0 EndX=121.894 EndY=-112.308 EndZ=0
  constraints (24):
    c: Coincident(g0,g1)
    c: Coincident(g1,g2)
    c: Coincident(g2,g3)
    c: Coincident(g3,g0)
    c: Vertical(g0)
    c: Vertical(g2)
    c: Horizontal(g1)
    c: Horizontal(g3)
    c: Coincident(g4,g5)
    c: Coincident(g5,g6)
    c: Coincident(g6,g7)
    c: Coincident(g7,g4)
    c: Vertical(g4)
    c: Vertical(g6)
    c: Horizontal(g5)
    c: Horizontal(g7)
    c: Coincident(g8,g9)
    c: Coincident(g9,g10)
    c: Coincident(g10,g11)
    c: Coincident(g11,g8)
    c: Vertical(g8)
    c: Vertical(g10)
    c: Horizontal(g9)
    c: Horizontal(g11)
FEATURE [PartDesign::Pad] Pad009
  BaseFeature = -> Pad008
  Direction = (0,0,1)
  Length = 0.2
  Length2 = 10
  Profile = -> Sketch012
  ReferenceAxis = -> Sketch012 [N_Axis]
  Suppressed = false
  Type = 0
FEATURE [PartDesign::Body] Body001
  AllowCompound = false
  Group = -> [ShapeBinder001,Sketch004,Pad003,Sketch005,Hole001,Sketch006,Pad004,Fillet002,Sketch008,Pad005,Sketch009,Pad006,Sketch010,Pad007,Sketch011,Pad008,Sketch012,Pad009]
  Origin = -> Origin069
  Placement = pos=(0,0,7.5) rot=(0,0,1;0rad)
  Tip = -> Pad009
